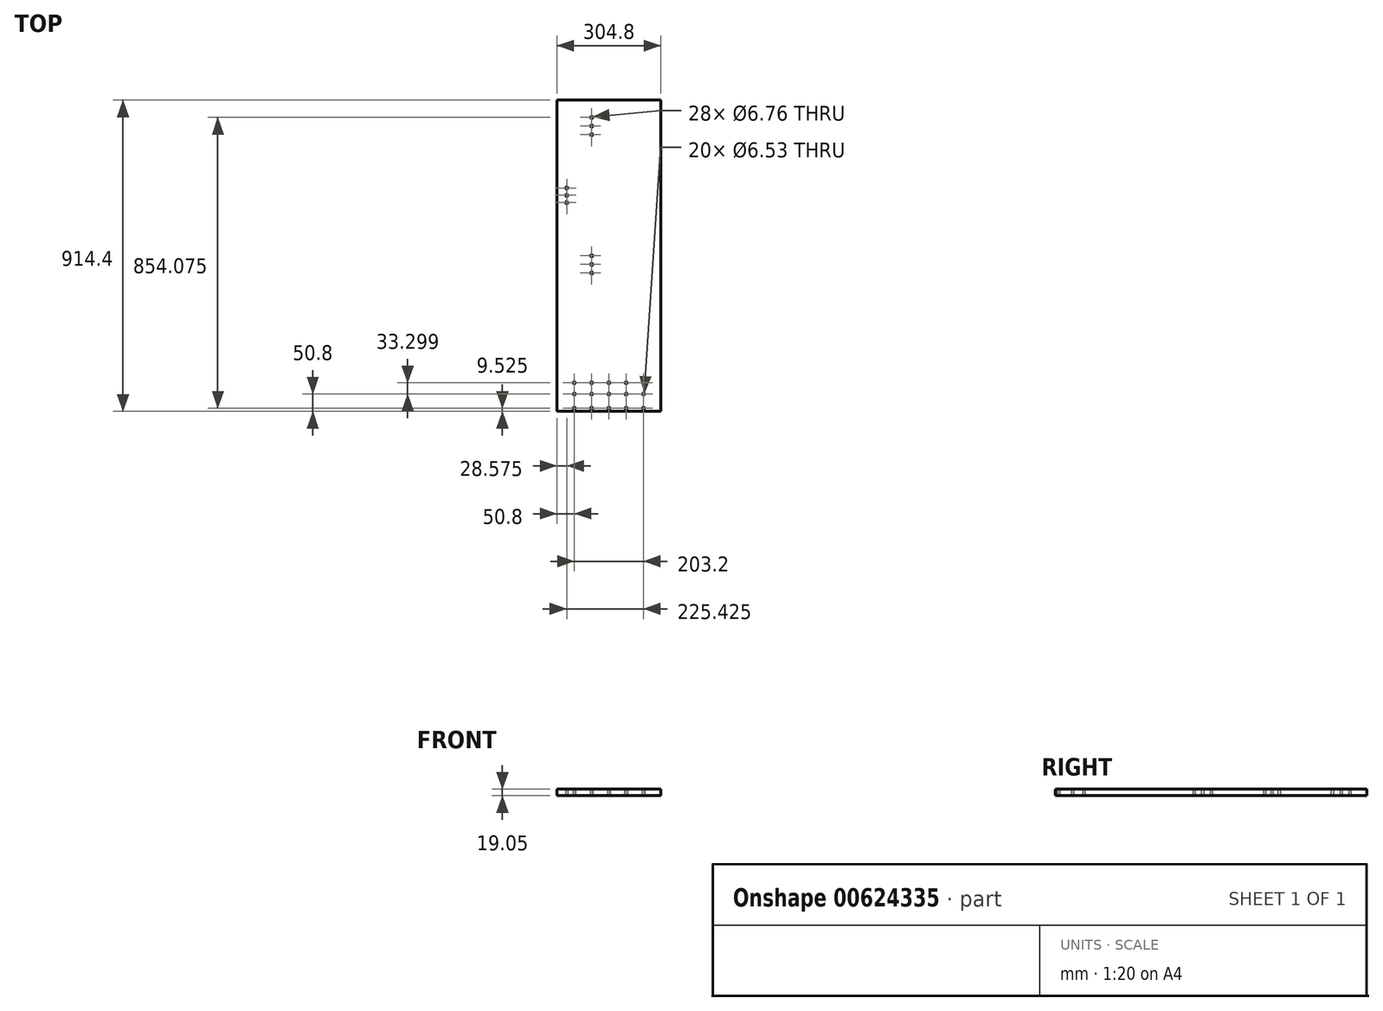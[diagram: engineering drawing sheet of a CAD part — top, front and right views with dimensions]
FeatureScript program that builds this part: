
annotation { "Feature Type Name" : "Feature", "Feature Type Description" : "" }
export const myFeature = defineFeature(function(context is Context, id is Id, definition is map)
    precondition{}
    {
        {
            var Q0;
            Q0=qCreatedBy(makeId("Top.planeOp"),FACE);
            var sketch = newSketch(context, id + "F0", { "sketchPlane" : qUnion([Q0])});
            skLineSegment(sketch, "E0.bottom", {"start": v(0, 0) * mm, "end": v(-304.8, 0) * mm});
            skLineSegment(sketch, "E0.top", {"start": v(0, 914.4) * mm, "end": v(-304.8, 914.4) * mm});
            skLineSegment(sketch, "E0.left", {"start": v(0, 0) * mm, "end": v(0, 914.4) * mm});
            skLineSegment(sketch, "E0.right", {"start": v(-304.8, 0) * mm, "end": v(-304.8, 914.4) * mm});
            skLineSegment(sketch, "E1", {"start": v(-203.2, 914.4) * mm, "end": v(-203.2, 0) * mm, "construction": true});
            skLineSegment(sketch, "E2", {"start": v(-304.8, 635) * mm, "end": v(0, 635) * mm, "construction": true});
            skCircle(sketch, "E3", {"center": v(-203.2, 863.6) * mm, "radius": 3.38 * mm});
            skCircle(sketch, "E4", {"center": v(-203.2, 838.2) * mm, "radius": 3.38 * mm});
            skCircle(sketch, "E5", {"center": v(-203.2, 812.8) * mm, "radius": 3.38 * mm});
            skCircle(sketch, "E6", {"center": v(-203.2, 457.2) * mm, "radius": 3.38 * mm});
            skCircle(sketch, "E7", {"center": v(-203.2, 431.8) * mm, "radius": 3.38 * mm});
            skCircle(sketch, "E8", {"center": v(-203.2, 406.4) * mm, "radius": 3.38 * mm});
            skLineSegment(sketch, "E9", {"start": v(-304.8, 9.52) * mm, "end": v(0, 9.52) * mm, "construction": true});
            skCircle(sketch, "E10", {"center": v(-254, 9.52) * mm, "radius": 3.38 * mm});
            skCircle(sketch, "E11.1.0.0", {"center": v(-203.2, 9.52) * mm, "radius": 3.38 * mm});
            skCircle(sketch, "E11.2.0.0", {"center": v(-152.4, 9.53) * mm, "radius": 3.38 * mm});
            skCircle(sketch, "E11.3.0.0", {"center": v(-101.6, 9.53) * mm, "radius": 3.38 * mm});
            skCircle(sketch, "E11.4.0.0", {"center": v(-50.8, 9.53) * mm, "radius": 3.38 * mm});
            skLineSegment(sketch, "E11.direction1", {"start": v(-254, 9.52) * mm, "end": v(-203.2, 9.52) * mm, "construction": true});
            skCircle(sketch, "E12", {"center": v(-276.23, 635) * mm, "radius": 3.38 * mm});
            skCircle(sketch, "E13", {"center": v(-276.23, 613.57) * mm, "radius": 3.38 * mm});
            skCircle(sketch, "E14", {"center": v(-276.23, 656.43) * mm, "radius": 3.38 * mm});
            skSolve(sketch);
        }
        {
            var Q0;
            Q0=makeQuery(id+"F0.imprint","IMPRINT",FACE,{"disambiguationData":[TD([[makeQuery(id+"F0.imprint","IMPRINT",EDGE,{"derivedFrom":sQuery(id+"F0.wireOp",EDGE,"E0.bottom")}),-1.0]])]});
            extrude(context, id + "F1", {"entities" : qUnion([Q0]), "depth" : 19.05 * mm, "offsetDistance" : 25.4 * mm});
        }
        {
            var Q0;
            Q0=makeQuery(id+"F1.opExtrude","CAP_FACE",FACE,{"disambiguationData":[OSD([sQuery(id+"F0.wireOp",EDGE,"E0.bottom"),sQuery(id+"F0.wireOp",EDGE,"E0.top"),sQuery(id+"F0.wireOp",EDGE,"E0.left"),sQuery(id+"F0.wireOp",EDGE,"E0.right"),sQuery(id+"F0.wireOp",EDGE,"E3"),sQuery(id+"F0.wireOp",EDGE,"E4"),sQuery(id+"F0.wireOp",EDGE,"E5"),sQuery(id+"F0.wireOp",EDGE,"E6"),sQuery(id+"F0.wireOp",EDGE,"E7"),sQuery(id+"F0.wireOp",EDGE,"E8"),sQuery(id+"F0.wireOp",EDGE,"E10"),sQuery(id+"F0.wireOp",EDGE,"E11.1.0.0"),sQuery(id+"F0.wireOp",EDGE,"E11.2.0.0"),sQuery(id+"F0.wireOp",EDGE,"E11.3.0.0"),sQuery(id+"F0.wireOp",EDGE,"E11.4.0.0")])],"isStart":false});
            var sketch = newSketch(context, id + "F2", { "sketchPlane" : qUnion([Q0])});
            skPoint(sketch, "E15", {"position": v(-254, 50.8) * mm});
            skPoint(sketch, "E16.0.1.0", {"position": v(-254, 84.1) * mm});
            skPoint(sketch, "E16.1.0.0", {"position": v(-203.2, 50.8) * mm});
            skPoint(sketch, "E16.1.1.0", {"position": v(-203.2, 84.1) * mm});
            skPoint(sketch, "E16.2.0.0", {"position": v(-152.4, 50.8) * mm});
            skPoint(sketch, "E16.2.1.0", {"position": v(-152.4, 84.1) * mm});
            skPoint(sketch, "E16.3.0.0", {"position": v(-101.6, 50.8) * mm});
            skPoint(sketch, "E16.3.1.0", {"position": v(-101.6, 84.1) * mm});
            skPoint(sketch, "E16.4.0.0", {"position": v(-50.8, 50.8) * mm});
            skPoint(sketch, "E16.4.1.0", {"position": v(-50.8, 84.1) * mm});
            skLineSegment(sketch, "E16.direction1", {"start": v(-254, 50.8) * mm, "end": v(-203.2, 50.8) * mm, "construction": true});
            skLineSegment(sketch, "E16.direction2", {"start": v(-254, 50.8) * mm, "end": v(-254, 84.1) * mm, "construction": true});
            skSolve(sketch);
        }
        {
            var Q0;
            Q0=sQuery(id+"F2.wireOp",VERTEX,"E16.0.1.0");
            var Q1;
            Q1=sQuery(id+"F2.wireOp",VERTEX,"E16.1.1.0");
            var Q2;
            Q2=sQuery(id+"F2.wireOp",VERTEX,"E16.2.1.0");
            var Q3;
            Q3=sQuery(id+"F2.wireOp",VERTEX,"E16.3.1.0");
            var Q4;
            Q4=sQuery(id+"F2.wireOp",VERTEX,"E16.4.1.0");
            var Q5;
            Q5=sQuery(id+"F2.wireOp",VERTEX,"E16.4.0.0");
            var Q6;
            Q6=sQuery(id+"F2.wireOp",VERTEX,"E16.3.0.0");
            var Q7;
            Q7=sQuery(id+"F2.wireOp",VERTEX,"E16.2.0.0");
            var Q8;
            Q8=sQuery(id+"F2.wireOp",VERTEX,"E16.1.0.0");
            var Q9;
            Q9=sQuery(id+"F2.wireOp",VERTEX,"E15");
            var Q10;
            Q10=makeQuery(id+"F1.opExtrude","SWEPT_BODY",BODY,{"disambiguationData":[OSD([sQuery(id+"F0.wireOp",EDGE,"E0.bottom"),sQuery(id+"F0.wireOp",EDGE,"E0.top"),sQuery(id+"F0.wireOp",EDGE,"E0.left"),sQuery(id+"F0.wireOp",EDGE,"E0.right"),sQuery(id+"F0.wireOp",EDGE,"E3"),sQuery(id+"F0.wireOp",EDGE,"E4"),sQuery(id+"F0.wireOp",EDGE,"E5"),sQuery(id+"F0.wireOp",EDGE,"E6"),sQuery(id+"F0.wireOp",EDGE,"E7"),sQuery(id+"F0.wireOp",EDGE,"E8"),sQuery(id+"F0.wireOp",EDGE,"E10"),sQuery(id+"F0.wireOp",EDGE,"E11.1.0.0"),sQuery(id+"F0.wireOp",EDGE,"E11.2.0.0"),sQuery(id+"F0.wireOp",EDGE,"E11.3.0.0"),sQuery(id+"F0.wireOp",EDGE,"E11.4.0.0")])]});
            hole(context, id + "F3", {"style" : HoleStyle.SIMPLE, "endStyle" : HoleEndStyle.THROUGH, "standardTappedOrClearance" : lookupTablePath({ "standard" : "ANSI", "fit" : "Close", "size" : "1/4", "type" : "Clearance" }), "standardBlindInLast" : lookupTablePath({ "fit" : "Close", "standard" : "ANSI", "size" : "1/4", "type" : "Clearance" }), "holeDiameter" : 6.53 * mm, "majorDiameter" : 6.35 * mm, "isTappedThrough" : true, "tappedDepth" : 12.7 * mm, "tapClearance" : 3, "startFromSketch" : true, "locations" : qUnion([Q0, Q1, Q2, Q3, Q4, Q5, Q6, Q7, Q8, Q9]), "scope" : qUnion([Q10])});
        }
        {
            var Q0;
            Q0=makeQuery(id+"F1.opExtrude","CAP_FACE",FACE,{"disambiguationData":[OSD([sQuery(id+"F0.wireOp",EDGE,"E0.bottom"),sQuery(id+"F0.wireOp",EDGE,"E0.top"),sQuery(id+"F0.wireOp",EDGE,"E0.left"),sQuery(id+"F0.wireOp",EDGE,"E0.right"),sQuery(id+"F0.wireOp",EDGE,"E3"),sQuery(id+"F0.wireOp",EDGE,"E4"),sQuery(id+"F0.wireOp",EDGE,"E5"),sQuery(id+"F0.wireOp",EDGE,"E6"),sQuery(id+"F0.wireOp",EDGE,"E7"),sQuery(id+"F0.wireOp",EDGE,"E8"),sQuery(id+"F0.wireOp",EDGE,"E10"),sQuery(id+"F0.wireOp",EDGE,"E11.1.0.0"),sQuery(id+"F0.wireOp",EDGE,"E11.2.0.0"),sQuery(id+"F0.wireOp",EDGE,"E11.3.0.0"),sQuery(id+"F0.wireOp",EDGE,"E11.4.0.0")])],"isStart":true});
            var sketch = newSketch(context, id + "F4", { "sketchPlane" : qUnion([Q0])});
            skLineSegment(sketch, "E17", {"start": v(-152.4, -50.8) * mm, "end": v(-152.4, -84.1) * mm, "construction": true});
            skPoint(sketch, "E18", {"position": v(-152.4, -67.45) * mm});
            skSolve(sketch);
        }
    });
